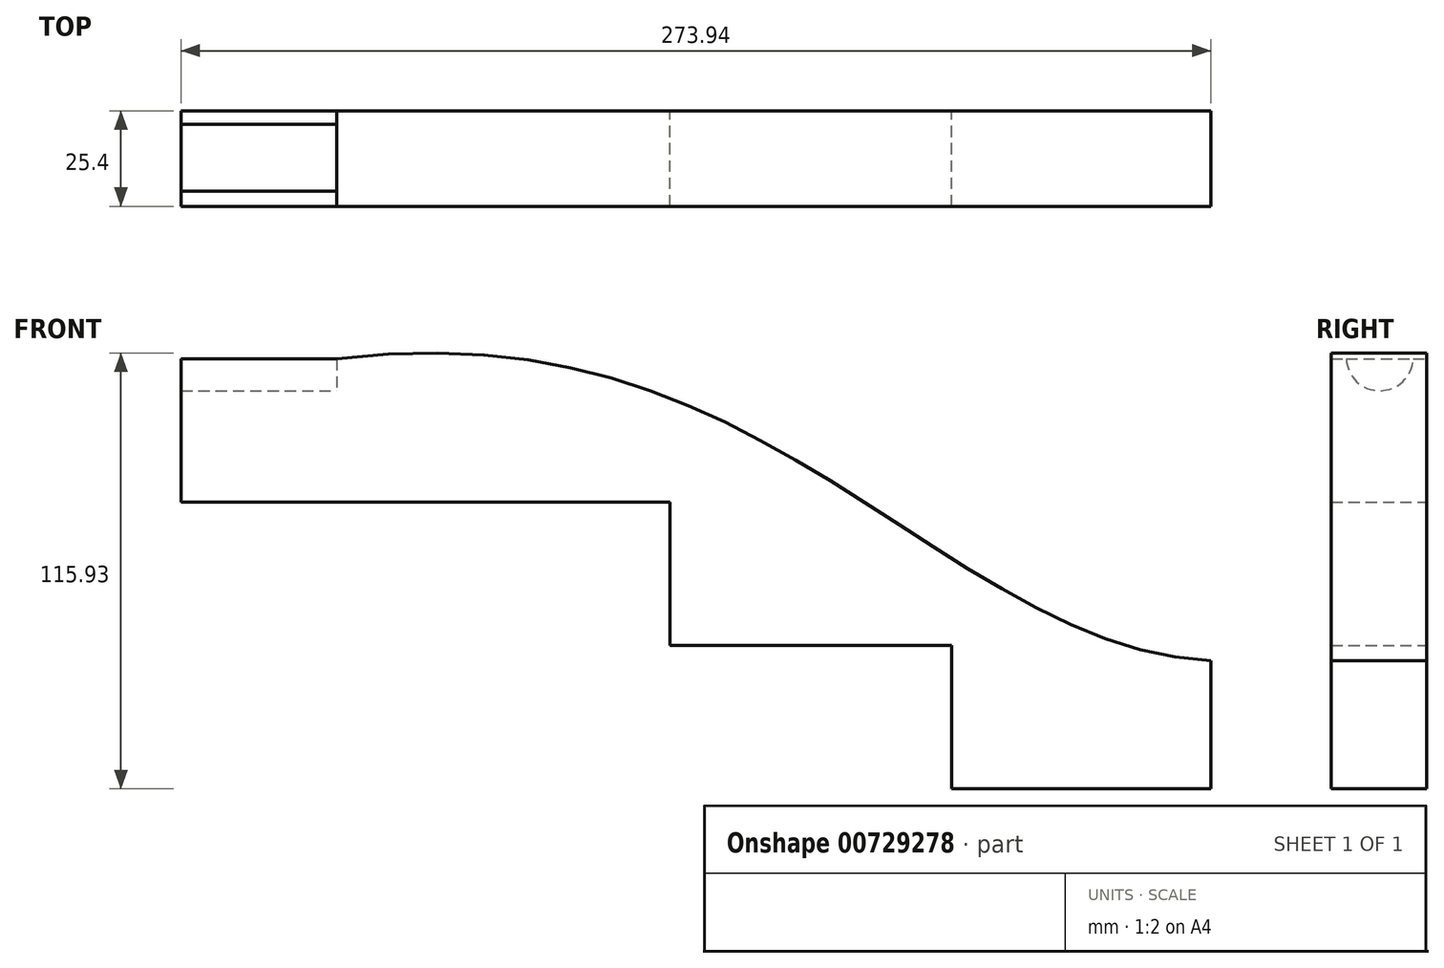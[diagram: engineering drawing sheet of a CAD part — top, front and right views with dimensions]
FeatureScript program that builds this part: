
annotation { "Feature Type Name" : "Feature", "Feature Type Description" : "" }
export const myFeature = defineFeature(function(context is Context, id is Id, definition is map)
    precondition{}
    {
        {
            var Q0;
            Q0=qCreatedBy(makeId("Front.planeOp"),FACE);
            var sketch = newSketch(context, id + "F0", { "sketchPlane" : qUnion([Q0])});
            skLineSegment(sketch, "E0", {"start": v(-181.43, 28.33) * mm, "end": v(-181.43, -9.77) * mm});
            skLineSegment(sketch, "E1", {"start": v(-181.43, -9.77) * mm, "end": v(-92.75, -9.77) * mm});
            skLineSegment(sketch, "E2", {"start": v(-92.75, -9.77) * mm, "end": v(-92.75, -47.87) * mm});
            skLineSegment(sketch, "E3", {"start": v(-92.75, -47.87) * mm, "end": v(-17.86, -47.87) * mm});
            skLineSegment(sketch, "E4", {"start": v(-17.86, -47.87) * mm, "end": v(-17.86, -85.97) * mm});
            skLineSegment(sketch, "E5", {"start": v(-17.86, -85.97) * mm, "end": v(51.11, -85.97) * mm});
            skLineSegment(sketch, "E6", {"start": v(51.11, -85.97) * mm, "end": v(51.11, -51.81) * mm});
            skFitSpline(sketch, "E7", {"points": [v(51.11, -51.81) * mm, v(-49.4, -4.52) * mm, v(-181.43, 28.33) * mm], "startDerivative": vector(-218.92, 7.01) * mm, "endDerivative": vector(-324.6, -40.58) * mm});
            skSolve(sketch);
        }
        {
            var Q0;
            Q0=makeQuery(id+"F0.imprint","IMPRINT",FACE,{"disambiguationData":[TD([[makeQuery(id+"F0.imprint","IMPRINT",EDGE,{"derivedFrom":sQuery(id+"F0.wireOp",EDGE,"E0")}),1.0]])]});
            extrude(context, id + "F1", {"entities" : qUnion([Q0]), "endBound" : BoundingType.SYMMETRIC, "depth" : 25.4 * mm, "offsetDistance" : 25.4 * mm});
        }
        {
            var Q0;
            Q0=makeQuery(id+"F1.opExtrude","SWEPT_FACE",FACE,{"disambiguationData":[OSD([sQuery(id+"F0.wireOp",EDGE,"E0")])]});
            var sketch = newSketch(context, id + "F2", { "sketchPlane" : qUnion([Q0])});
            skArc(sketch, "E8", {"start": v(-9.13, 28.33) * mm, "mid": v(-0.22, 19.91) * mm, "end": v(8.69, 28.33) * mm});
            skSolve(sketch);
        }
        {
            var Q0;
            {var subQ3=sQuery(id+"F2.wireOp",EDGE,"E8");Q0=makeQuery(id+"F2.imprint","IMPRINT",FACE,{"disambiguationData":[TD([[makeQuery(id+"F2.imprint","IMPRINT",EDGE,{"derivedFrom":subQ3}),-1.0]])]});}
            extrude(context, id + "F3", {"entities" : qUnion([Q0]), "operationType" : NewBodyOperationType.ADD, "depth" : 41.4 * mm, "offsetDistance" : 25.4 * mm});
        }
    });
